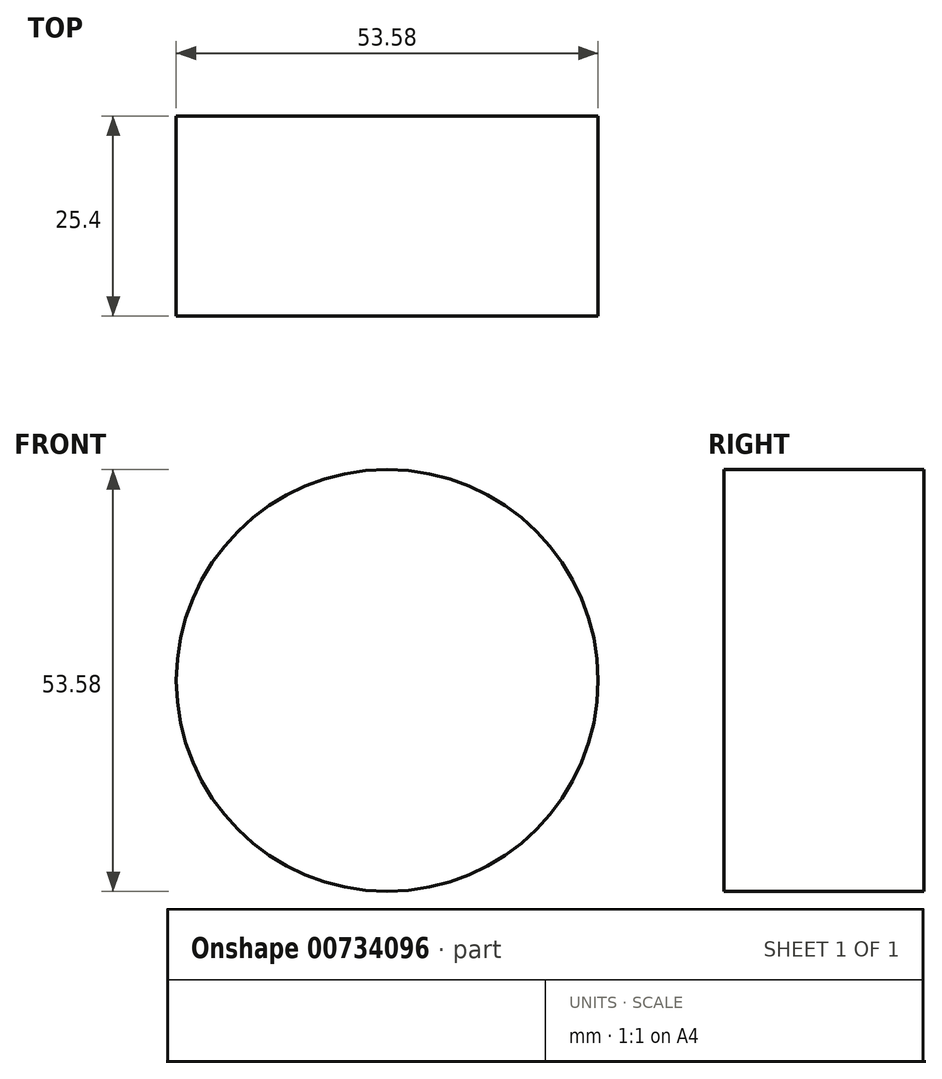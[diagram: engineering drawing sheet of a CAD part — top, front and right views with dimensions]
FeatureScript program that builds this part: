
annotation { "Feature Type Name" : "Feature", "Feature Type Description" : "" }
export const myFeature = defineFeature(function(context is Context, id is Id, definition is map)
    precondition{}
    {
        {
            var Q0;
            Q0=qCreatedBy(makeId("Front.planeOp"),FACE);
            var sketch = newSketch(context, id + "F0", { "sketchPlane" : qUnion([Q0])});
            skCircle(sketch, "E0", {"center": v(-27.2, 27.77) * mm, "radius": 26.8 * mm});
            skSolve(sketch);
        }
        {
            var Q0;
            Q0=makeQuery(id+"F0.imprint","IMPRINT",FACE,{"disambiguationData":[TD([[makeQuery(id+"F0.imprint","IMPRINT",EDGE,{"derivedFrom":sQuery(id+"F0.wireOp",EDGE,"E0")}),1.0]])]});
            extrude(context, id + "F1", {"entities" : qUnion([Q0]), "depth" : 25.4 * mm, "offsetDistance" : 25.4 * mm});
        }
    });
